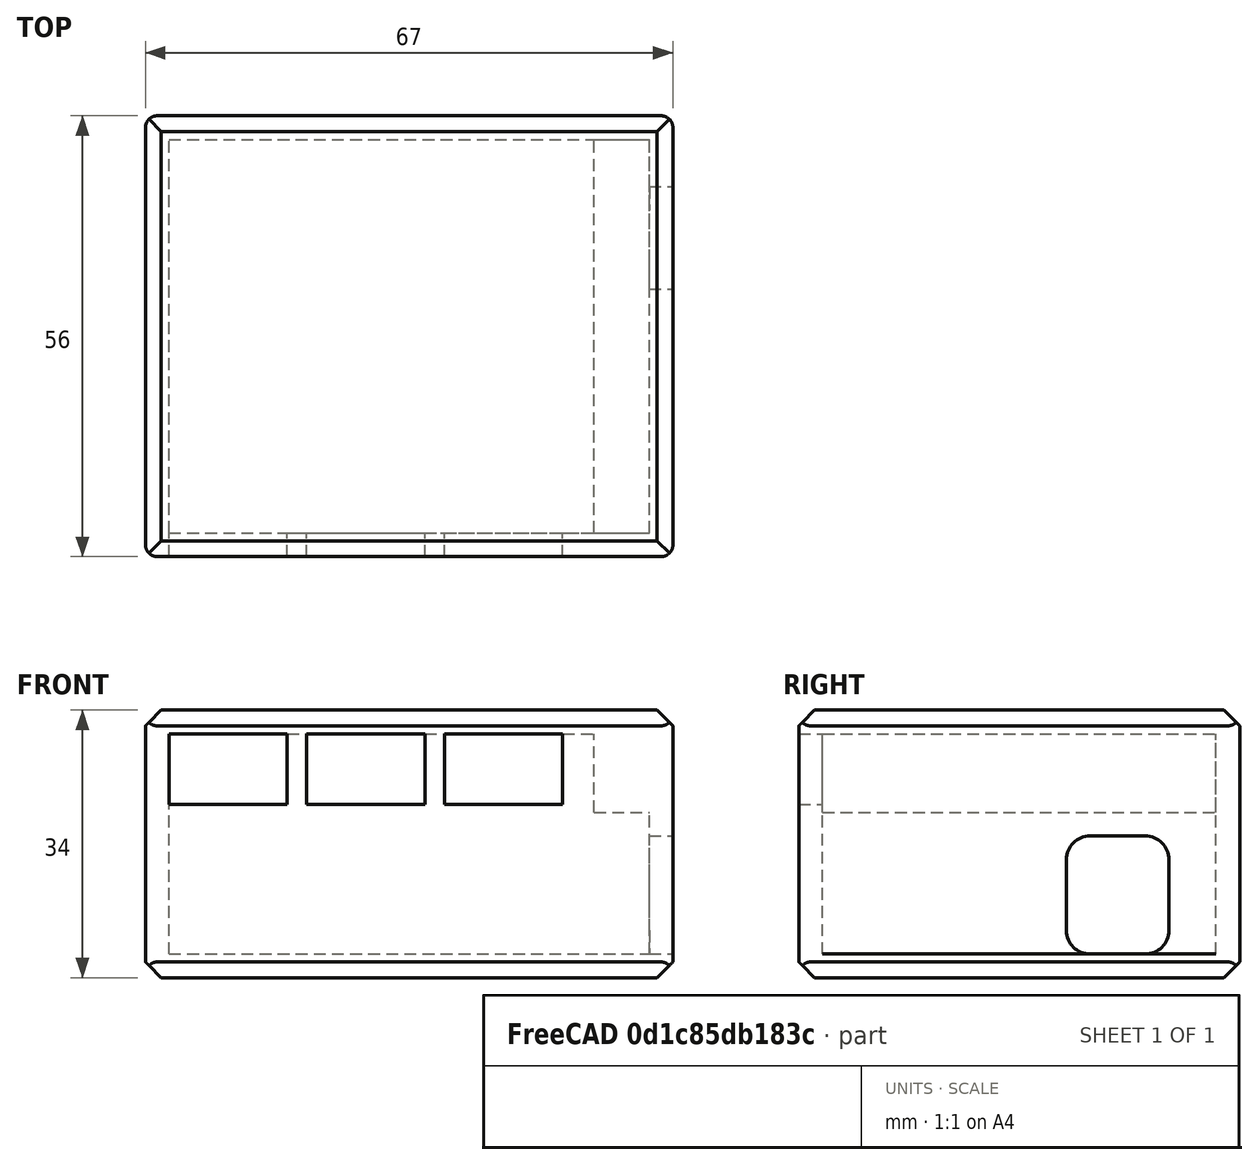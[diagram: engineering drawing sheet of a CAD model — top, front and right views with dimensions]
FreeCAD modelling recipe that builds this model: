
FCSTD DOCUMENT  (FreeCAD 0.18.4R)
Label: case
License: All rights reserved
LicenseURL: http://en.wikipedia.org/wiki/All_rights_reserved
objects: Part::Box×7, Part::Cut×2, Part::Fillet×2, Part::MultiFuse×1, Part::Chamfer×1
note: 13 computed .brp shape members not serialized (recipe doc carries the construction recipe); baked Part::Feature solids carry a one-line shape summary decoded from their .brp

FEATURE [Part::Box] Box  label="Cube"
  AttacherType = Attacher::AttachEngine3D
  Height = 28
  Length = 61
  Width = 50
FEATURE [Part::Box] Box001  label="Cube001"
  AttacherType = Attacher::AttachEngine3D
  Height = 15
  Length = 5
  Placement = pos=(61,31,0) rot=(0,0,1;0rad)
  Width = 13
FEATURE [Part::Box] Box002  label="Cube002"
  AttacherType = Attacher::AttachEngine3D
  Height = 9
  Length = 15
  Placement = pos=(0,-5,19) rot=(0,0,1;0rad)
  Width = 5
FEATURE [Part::Box] Box003  label="Cube003"
  AttacherType = Attacher::AttachEngine3D
  Height = 9
  Length = 15
  Placement = pos=(17.5,-5,19) rot=(0,0,1;0rad)
  Width = 5
FEATURE [Part::Box] Box004  label="Cube004"
  AttacherType = Attacher::AttachEngine3D
  Height = 9
  Length = 15
  Placement = pos=(35,-5,19) rot=(0,0,1;0rad)
  Width = 5
FEATURE [Part::Box] Box005  label="Cube005"
  AttacherType = Attacher::AttachEngine3D
  Height = 10
  Length = 7
  Placement = pos=(54,0,18) rot=(0,0,1;0rad)
  Width = 50
FEATURE [Part::Cut] Cut
  Base = -> Box
  Tool = -> Box005
FEATURE [Part::Box] Box006  label="Cube006"
  AttacherType = Attacher::AttachEngine3D
  Height = 34
  Length = 67
  Placement = pos=(-3,-3,-3) rot=(0,0,1;0rad)
  Width = 56
FEATURE [Part::MultiFuse] Fusion
  Shapes = -> [Box001,Box003,Box002,Cut,Box004]
FEATURE [Part::Cut] Cut001
  Base = -> Box006
  Tool = -> Fusion
FEATURE [Part::Fillet] Fillet
  Base = -> Cut001
  Edges = 4 edges r=3: [Edge53,Edge54,Edge56,Edge58]
FEATURE [Part::Chamfer] Chamfer
  Base = -> Fillet
  Edges = 8 edges r=2: [Edge10,Edge11,Edge31,Edge33,Edge46,Edge47,Edge48,Edge49]
FEATURE [Part::Fillet] Fillet001
  Base = -> Chamfer
  Edges = 4 edges r=1.5: [Edge1,Edge4,Edge15,Edge36]
